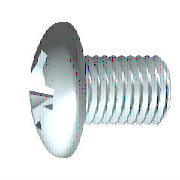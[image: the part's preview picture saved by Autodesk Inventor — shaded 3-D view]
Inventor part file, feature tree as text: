
AUTODESK INVENTOR PART (.ipt)
format: ipt  version: 2013 (Build 170138000, 138)  size: 302,080 bytes
history: native  units: mm (DEFAULTED — no unit token found)
features: extrude x2, other x1, plane x1
ambient origin geometry x7: Origin, YZ Plane, XZ Plane, X Axis, Y Axis, Z Axis, Center Point
bodies: Solid1 (feature_tree), Body (feature_tree)
feature tree (4):
  extrude  "Slot"  Depth=1.524mm
  other  "Cut"
  extrude  "Star Cut"  Depth=1.016mm
  plane  "Work Plane3"
